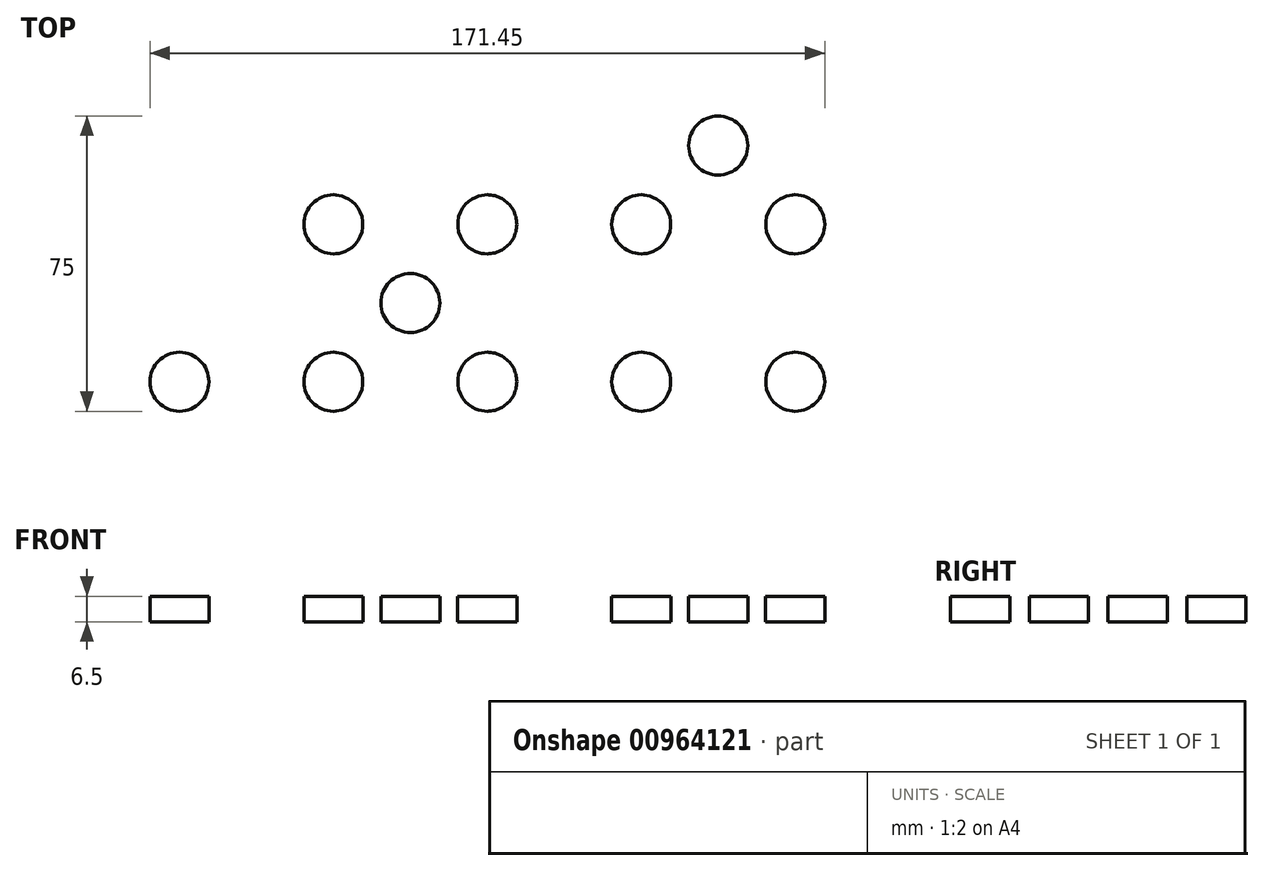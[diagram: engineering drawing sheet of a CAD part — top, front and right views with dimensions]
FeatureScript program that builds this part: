
annotation { "Feature Type Name" : "Feature", "Feature Type Description" : "" }
export const myFeature = defineFeature(function(context is Context, id is Id, definition is map)
    precondition{}
    {
        {
            var Q0;
            Q0=qCreatedBy(makeId("Top.planeOp"),FACE);
            var sketch = newSketch(context, id + "F0", { "sketchPlane" : qUnion([Q0])});
            skLineSegment(sketch, "E0.bottom", {"start": v(-100, 55) * mm, "end": v(100, 55) * mm});
            skLineSegment(sketch, "E0.top", {"start": v(-100, -55) * mm, "end": v(100, -55) * mm});
            skLineSegment(sketch, "E0.left", {"start": v(-100, 55) * mm, "end": v(-100, -55) * mm});
            skLineSegment(sketch, "E0.right", {"start": v(100, 55) * mm, "end": v(100, -55) * mm});
            skPoint(sketch, "E0.middle", {"position": v(0, 0) * mm});
            skSolve(sketch);
        }
        {
            var Q0;
            Q0=makeQuery(id+"F0.imprint","IMPRINT",FACE,{"disambiguationData":[TD([[makeQuery(id+"F0.imprint","IMPRINT",EDGE,{"derivedFrom":sQuery(id+"F0.wireOp",EDGE,"E0.bottom")}),-1.0]])]});
            extrude(context, id + "F1", {"entities" : qUnion([Q0]), "depth" : 6.5 * mm, "offsetDistance" : 25 * mm});
        }
        {
            var Q0;
            Q0=makeQuery(id+"F1.opExtrude","SWEPT_FACE",FACE,{"disambiguationData":[OSD([sQuery(id+"F0.wireOp",EDGE,"E0.left")])]});
            var sketch = newSketch(context, id + "F2", { "sketchPlane" : qUnion([Q0])});
            skLineSegment(sketch, "E1", {"start": v(-55, 3.25) * mm, "end": v(-35, 3.25) * mm});
            skLineSegment(sketch, "E2", {"start": v(-35, 3.25) * mm, "end": v(0, 3.25) * mm});
            skLineSegment(sketch, "E3", {"start": v(0, 3.25) * mm, "end": v(35, 3.25) * mm});
            skLineSegment(sketch, "E4", {"start": v(35, 3.25) * mm, "end": v(55, 3.25) * mm});
            skLineSegment(sketch, "E5.bottom", {"start": v(-39.75, 6.5) * mm, "end": v(-30.25, 6.5) * mm});
            skLineSegment(sketch, "E5.top", {"start": v(-39.75, 0) * mm, "end": v(-30.25, 0) * mm});
            skLineSegment(sketch, "E5.left", {"start": v(-39.75, 6.5) * mm, "end": v(-39.75, 0) * mm});
            skLineSegment(sketch, "E5.right", {"start": v(-30.25, 6.5) * mm, "end": v(-30.25, 0) * mm});
            skPoint(sketch, "E5.middle", {"position": v(-35, 3.25) * mm});
            skLineSegment(sketch, "E6.bottom", {"start": v(-4.75, 6.5) * mm, "end": v(4.75, 6.5) * mm});
            skLineSegment(sketch, "E6.top", {"start": v(-4.75, 0) * mm, "end": v(4.75, 0) * mm});
            skLineSegment(sketch, "E6.left", {"start": v(-4.75, 6.5) * mm, "end": v(-4.75, 0) * mm});
            skLineSegment(sketch, "E6.right", {"start": v(4.75, 6.5) * mm, "end": v(4.75, 0) * mm});
            skPoint(sketch, "E6.middle", {"position": v(0, 3.25) * mm});
            skLineSegment(sketch, "E7.bottom", {"start": v(39.75, 6.5) * mm, "end": v(30.25, 6.5) * mm});
            skLineSegment(sketch, "E7.top", {"start": v(39.75, 0) * mm, "end": v(30.25, 0) * mm});
            skLineSegment(sketch, "E7.left", {"start": v(39.75, 6.5) * mm, "end": v(39.75, 0) * mm});
            skLineSegment(sketch, "E7.right", {"start": v(30.25, 6.5) * mm, "end": v(30.25, 0) * mm});
            skPoint(sketch, "E7.middle", {"position": v(35, 3.25) * mm});
            skSolve(sketch);
        }
        {
            var Q0;
            {var subQ0=sQuery(id+"F2.wireOp",EDGE,"E5.bottom");Q0=makeQuery(id+"F2.imprint","IMPRINT",FACE,{"disambiguationData":[TD([[makeQuery(id+"F2.imprint","IMPRINT",EDGE,{"derivedFrom":subQ0}),-1.0]])]});}
            var Q1;
            {var subQ1=sQuery(id+"F2.wireOp",EDGE,"E5.top");Q1=makeQuery(id+"F2.imprint","IMPRINT",FACE,{"disambiguationData":[TD([[makeQuery(id+"F2.imprint","IMPRINT",EDGE,{"derivedFrom":subQ1}),1.0]])]});}
            var Q2;
            {var subQ1=sQuery(id+"F2.wireOp",EDGE,"E6.bottom");Q2=makeQuery(id+"F2.imprint","IMPRINT",FACE,{"disambiguationData":[TD([[makeQuery(id+"F2.imprint","IMPRINT",EDGE,{"derivedFrom":subQ1}),-1.0]])]});}
            var Q3;
            {var subQ0=sQuery(id+"F2.wireOp",EDGE,"E6.top");Q3=makeQuery(id+"F2.imprint","IMPRINT",FACE,{"disambiguationData":[TD([[makeQuery(id+"F2.imprint","IMPRINT",EDGE,{"derivedFrom":subQ0}),1.0]])]});}
            var Q4;
            {var subQ1=sQuery(id+"F2.wireOp",EDGE,"E7.bottom");Q4=makeQuery(id+"F2.imprint","IMPRINT",FACE,{"disambiguationData":[TD([[makeQuery(id+"F2.imprint","IMPRINT",EDGE,{"derivedFrom":subQ1}),-1.0]])]});}
            var Q5;
            {var subQ1=sQuery(id+"F2.wireOp",EDGE,"E7.top");Q5=makeQuery(id+"F2.imprint","IMPRINT",FACE,{"disambiguationData":[TD([[makeQuery(id+"F2.imprint","IMPRINT",EDGE,{"derivedFrom":subQ1}),1.0]])]});}
            extrude(context, id + "F3", {"entities" : qUnion([Q0, Q1, Q2, Q3, Q4, Q5]), "operationType" : NewBodyOperationType.ADD, "depth" : 6 * mm, "offsetDistance" : 25 * mm});
        }
        {
            var Q0;
            Q0=makeQuery(id+"F1.opExtrude","SWEPT_FACE",FACE,{"disambiguationData":[OSD([sQuery(id+"F0.wireOp",EDGE,"E0.right")])]});
            var sketch = newSketch(context, id + "F4", { "sketchPlane" : qUnion([Q0])});
            skLineSegment(sketch, "E8", {"start": v(-55, 3.25) * mm, "end": v(-35, 3.25) * mm});
            skLineSegment(sketch, "E9", {"start": v(-35, 3.25) * mm, "end": v(0, 3.25) * mm});
            skLineSegment(sketch, "E10", {"start": v(0, 3.25) * mm, "end": v(35, 3.25) * mm});
            skLineSegment(sketch, "E11.bottom", {"start": v(-39.75, 6.5) * mm, "end": v(-30.25, 6.5) * mm});
            skLineSegment(sketch, "E11.top", {"start": v(-39.75, 0) * mm, "end": v(-30.25, 0) * mm});
            skLineSegment(sketch, "E11.left", {"start": v(-39.75, 6.5) * mm, "end": v(-39.75, 0) * mm});
            skLineSegment(sketch, "E11.right", {"start": v(-30.25, 6.5) * mm, "end": v(-30.25, 0) * mm});
            skPoint(sketch, "E11.middle", {"position": v(-35, 3.25) * mm});
            skLineSegment(sketch, "E12.bottom", {"start": v(-4.75, 6.5) * mm, "end": v(4.75, 6.5) * mm});
            skLineSegment(sketch, "E12.top", {"start": v(-4.75, 0) * mm, "end": v(4.75, 0) * mm});
            skLineSegment(sketch, "E12.left", {"start": v(-4.75, 6.5) * mm, "end": v(-4.75, 0) * mm});
            skLineSegment(sketch, "E12.right", {"start": v(4.75, 6.5) * mm, "end": v(4.75, 0) * mm});
            skPoint(sketch, "E12.middle", {"position": v(0, 3.25) * mm});
            skLineSegment(sketch, "E13.bottom", {"start": v(39.75, 6.5) * mm, "end": v(30.25, 6.5) * mm});
            skLineSegment(sketch, "E13.top", {"start": v(39.75, 0) * mm, "end": v(30.25, 0) * mm});
            skLineSegment(sketch, "E13.left", {"start": v(39.75, 6.5) * mm, "end": v(39.75, 0) * mm});
            skLineSegment(sketch, "E13.right", {"start": v(30.25, 6.5) * mm, "end": v(30.25, 0) * mm});
            skPoint(sketch, "E13.middle", {"position": v(35, 3.25) * mm});
            skSolve(sketch);
        }
        {
            var Q0;
            {var subQ1=sQuery(id+"F4.wireOp",EDGE,"E11.bottom");Q0=makeQuery(id+"F4.imprint","IMPRINT",FACE,{"disambiguationData":[TD([[makeQuery(id+"F4.imprint","IMPRINT",EDGE,{"derivedFrom":subQ1}),1.0]])]});}
            var Q1;
            {var subQ1=sQuery(id+"F4.wireOp",EDGE,"E11.top");Q1=makeQuery(id+"F4.imprint","IMPRINT",FACE,{"disambiguationData":[TD([[makeQuery(id+"F4.imprint","IMPRINT",EDGE,{"derivedFrom":subQ1}),-1.0]])]});}
            var Q2;
            {var subQ0=sQuery(id+"F4.wireOp",EDGE,"E12.bottom");Q2=makeQuery(id+"F4.imprint","IMPRINT",FACE,{"disambiguationData":[TD([[makeQuery(id+"F4.imprint","IMPRINT",EDGE,{"derivedFrom":subQ0}),1.0]])]});}
            var Q3;
            {var subQ1=sQuery(id+"F4.wireOp",EDGE,"E12.top");Q3=makeQuery(id+"F4.imprint","IMPRINT",FACE,{"disambiguationData":[TD([[makeQuery(id+"F4.imprint","IMPRINT",EDGE,{"derivedFrom":subQ1}),-1.0]])]});}
            var Q4;
            {var subQ1=sQuery(id+"F4.wireOp",EDGE,"E13.bottom");Q4=makeQuery(id+"F4.imprint","IMPRINT",FACE,{"disambiguationData":[TD([[makeQuery(id+"F4.imprint","IMPRINT",EDGE,{"derivedFrom":subQ1}),1.0]])]});}
            extrude(context, id + "F5", {"entities" : qUnion([Q0, Q1, Q2, Q3, Q4]), "operationType" : NewBodyOperationType.ADD, "depth" : 6 * mm, "offsetDistance" : 25 * mm});
        }
        {
            var Q0;
            Q0=makeQuery(id+"F5.boolean.opBoolean","MERGE",FACE,{"derivedFrom":[makeQuery(id+"F3.boolean.opBoolean","MERGE",FACE,{"derivedFrom":[makeQuery(id+"F1.opExtrude","CAP_FACE",FACE,{"disambiguationData":[OSD([sQuery(id+"F0.wireOp",EDGE,"E0.bottom"),sQuery(id+"F0.wireOp",EDGE,"E0.top"),sQuery(id+"F0.wireOp",EDGE,"E0.left"),sQuery(id+"F0.wireOp",EDGE,"E0.right")])],"isStart":false}),makeQuery(id+"F3.opExtrude","SWEPT_FACE",FACE,{"disambiguationData":[OSD([sQuery(id+"F2.wireOp",EDGE,"E5.bottom")])]}),makeQuery(id+"F3.opExtrude","SWEPT_FACE",FACE,{"disambiguationData":[OSD([sQuery(id+"F2.wireOp",EDGE,"E6.bottom")])]}),makeQuery(id+"F3.opExtrude","SWEPT_FACE",FACE,{"disambiguationData":[OSD([sQuery(id+"F2.wireOp",EDGE,"E7.bottom")])]})]}),makeQuery(id+"F5.opExtrude","SWEPT_FACE",FACE,{"disambiguationData":[OSD([sQuery(id+"F4.wireOp",EDGE,"E11.bottom")])]}),makeQuery(id+"F5.opExtrude","SWEPT_FACE",FACE,{"disambiguationData":[OSD([sQuery(id+"F4.wireOp",EDGE,"E12.bottom")])]}),makeQuery(id+"F5.opExtrude","SWEPT_FACE",FACE,{"disambiguationData":[OSD([sQuery(id+"F4.wireOp",EDGE,"E13.bottom")])]})]});
            var sketch = newSketch(context, id + "F6", { "sketchPlane" : qUnion([Q0])});
            skLineSegment(sketch, "E14", {"start": v(-88, 55) * mm, "end": v(-88, 40) * mm});
            skLineSegment(sketch, "E15", {"start": v(-88, 40) * mm, "end": v(-88, 20) * mm});
            skLineSegment(sketch, "E16", {"start": v(-88, 20) * mm, "end": v(-88, 0) * mm});
            skLineSegment(sketch, "E17", {"start": v(-88, 0) * mm, "end": v(-88, -20) * mm});
            skLineSegment(sketch, "E18", {"start": v(-88, -20) * mm, "end": v(-88, -40) * mm});
            skCircle(sketch, "E19", {"center": v(-88, 40) * mm, "radius": 7.5 * mm});
            skCircle(sketch, "E20", {"center": v(-88, 20) * mm, "radius": 7.5 * mm});
            skCircle(sketch, "E21", {"center": v(-88, 0) * mm, "radius": 7.5 * mm});
            skCircle(sketch, "E22", {"center": v(-88, -20) * mm, "radius": 7.5 * mm});
            skCircle(sketch, "E23", {"center": v(-88, -40) * mm, "radius": 7.5 * mm});
            skLineSegment(sketch, "E24", {"start": v(-68.44, 55) * mm, "end": v(-68.44, -55) * mm});
            skLineSegment(sketch, "E25", {"start": v(-48.89, 55) * mm, "end": v(-48.89, -55) * mm});
            skLineSegment(sketch, "E26", {"start": v(-29.33, 55) * mm, "end": v(-29.33, -55) * mm});
            skLineSegment(sketch, "E27", {"start": v(-9.78, -55) * mm, "end": v(-9.78, 55) * mm});
            skLineSegment(sketch, "E28", {"start": v(9.78, 55) * mm, "end": v(9.78, -55) * mm});
            skLineSegment(sketch, "E29", {"start": v(29.33, -55) * mm, "end": v(29.33, 55) * mm});
            skLineSegment(sketch, "E30", {"start": v(68.44, 55) * mm, "end": v(68.44, -55) * mm});
            skLineSegment(sketch, "E31", {"start": v(48.89, 55) * mm, "end": v(48.89, -55) * mm});
            skLineSegment(sketch, "E32", {"start": v(88, 55) * mm, "end": v(88, -55) * mm});
            skCircle(sketch, "E33", {"center": v(-68.44, 40) * mm, "radius": 7.99 * mm});
            skCircle(sketch, "E34", {"center": v(-68.44, 20) * mm, "radius": 7.5 * mm});
            skCircle(sketch, "E35", {"center": v(-68.44, 0) * mm, "radius": 7.5 * mm});
            skCircle(sketch, "E36", {"center": v(-68.44, -20) * mm, "radius": 7.5 * mm});
            skCircle(sketch, "E37", {"center": v(-68.44, -40) * mm, "radius": 7.5 * mm});
            skCircle(sketch, "E38.MirrorC", {"center": v(-48.89, 40) * mm, "radius": 7.5 * mm});
            skCircle(sketch, "E39.MirrorC", {"center": v(-48.89, 20) * mm, "radius": 7.5 * mm});
            skCircle(sketch, "E40.MirrorC", {"center": v(-48.89, 0) * mm, "radius": 7.5 * mm});
            skCircle(sketch, "E41.MirrorC", {"center": v(-48.89, -20) * mm, "radius": 7.5 * mm});
            skCircle(sketch, "E42.MirrorC", {"center": v(-48.89, -40) * mm, "radius": 7.5 * mm});
            skCircle(sketch, "E43.MirrorC", {"center": v(-29.33, 40) * mm, "radius": 7.99 * mm});
            skCircle(sketch, "E44.MirrorC", {"center": v(-29.33, 20) * mm, "radius": 7.5 * mm});
            skCircle(sketch, "E45.MirrorC", {"center": v(-29.33, 0) * mm, "radius": 7.5 * mm});
            skCircle(sketch, "E46.MirrorC", {"center": v(-29.33, -20) * mm, "radius": 7.5 * mm});
            skCircle(sketch, "E47.MirrorC", {"center": v(-29.33, -40) * mm, "radius": 7.5 * mm});
            skCircle(sketch, "E48.MirrorC", {"center": v(-9.78, 40) * mm, "radius": 7.5 * mm});
            skCircle(sketch, "E49.MirrorC", {"center": v(-9.78, 20) * mm, "radius": 7.5 * mm});
            skCircle(sketch, "E50.MirrorC", {"center": v(-9.78, 0) * mm, "radius": 7.5 * mm});
            skCircle(sketch, "E51.MirrorC", {"center": v(-9.78, -40) * mm, "radius": 7.5 * mm});
            skCircle(sketch, "E52.MirrorC", {"center": v(-9.78, -20) * mm, "radius": 7.5 * mm});
            skCircle(sketch, "E53.MirrorC", {"center": v(29.33, 40) * mm, "radius": 7.5 * mm});
            skCircle(sketch, "E54.MirrorC", {"center": v(29.33, 20) * mm, "radius": 7.5 * mm});
            skCircle(sketch, "E55.MirrorC", {"center": v(29.33, 0) * mm, "radius": 7.5 * mm});
            skCircle(sketch, "E56.MirrorC", {"center": v(29.33, -20) * mm, "radius": 7.5 * mm});
            skCircle(sketch, "E57.MirrorC", {"center": v(29.33, -40) * mm, "radius": 7.5 * mm});
            skCircle(sketch, "E58.MirrorC", {"center": v(9.78, 20) * mm, "radius": 7.5 * mm});
            skCircle(sketch, "E59.MirrorC", {"center": v(9.78, 0) * mm, "radius": 7.5 * mm});
            skCircle(sketch, "E60.MirrorC", {"center": v(9.78, 40) * mm, "radius": 7.99 * mm});
            skCircle(sketch, "E61.MirrorC", {"center": v(9.78, -20) * mm, "radius": 7.5 * mm});
            skCircle(sketch, "E62.MirrorC", {"center": v(9.78, -40) * mm, "radius": 7.5 * mm});
            skCircle(sketch, "E63.MirrorC", {"center": v(48.89, 40) * mm, "radius": 7.99 * mm});
            skCircle(sketch, "E64.MirrorC", {"center": v(48.89, 20) * mm, "radius": 7.5 * mm});
            skCircle(sketch, "E65.MirrorC", {"center": v(48.89, 0) * mm, "radius": 7.5 * mm});
            skCircle(sketch, "E66.MirrorC", {"center": v(48.89, -20) * mm, "radius": 7.5 * mm});
            skCircle(sketch, "E67.MirrorC", {"center": v(48.89, -40) * mm, "radius": 7.5 * mm});
            skCircle(sketch, "E68.MirrorC", {"center": v(68.44, 40) * mm, "radius": 7.5 * mm});
            skCircle(sketch, "E69.MirrorC", {"center": v(68.44, 20) * mm, "radius": 7.5 * mm});
            skCircle(sketch, "E70.MirrorC", {"center": v(68.44, 0) * mm, "radius": 7.5 * mm});
            skCircle(sketch, "E71.MirrorC", {"center": v(68.44, -20) * mm, "radius": 7.5 * mm});
            skCircle(sketch, "E72.MirrorC", {"center": v(68.44, -40) * mm, "radius": 7.5 * mm});
            skCircle(sketch, "E73.MirrorC", {"center": v(88, 40) * mm, "radius": 7.99 * mm});
            skCircle(sketch, "E74.MirrorC", {"center": v(88, 20) * mm, "radius": 7.5 * mm});
            skCircle(sketch, "E75.MirrorC", {"center": v(88, 0) * mm, "radius": 7.5 * mm});
            skCircle(sketch, "E76.MirrorC", {"center": v(88, -20) * mm, "radius": 7.5 * mm});
            skCircle(sketch, "E77.MirrorC", {"center": v(88, -40) * mm, "radius": 7.5 * mm});
            skSolve(sketch);
        }
        {
            var Q0;
            {var subQ0=sQuery(id+"F6.wireOp",EDGE,"E15");var subQ1=sQuery(id+"F6.wireOp",EDGE,"E14");var subQ2=makeQuery(id+"F6.imprint","INTERSECT",VERTEX,{"derivedFrom":[subQ1,subQ0]});Q0=makeQuery(id+"F6.imprint","IMPRINT",FACE,{"disambiguationData":[TD([[makeQuery(id+"F6.imprint","IMPRINT",EDGE,{"disambiguationData":[TD([[subQ2,1.0]])],"derivedFrom":subQ1}),-1.0]])]});}
            var Q1;
            {var subQ0=sQuery(id+"F6.wireOp",EDGE,"E15");var subQ1=sQuery(id+"F6.wireOp",EDGE,"E14");var subQ2=makeQuery(id+"F6.imprint","INTERSECT",VERTEX,{"derivedFrom":[subQ1,subQ0]});Q1=makeQuery(id+"F6.imprint","IMPRINT",FACE,{"disambiguationData":[TD([[makeQuery(id+"F6.imprint","IMPRINT",EDGE,{"disambiguationData":[TD([[subQ2,1.0]])],"derivedFrom":subQ1}),1.0]])]});}
            var Q2;
            {var subQ0=sQuery(id+"F6.wireOp",EDGE,"E33");var subQ1=sQuery(id+"F6.wireOp",EDGE,"E24");var subQ2=makeQuery(id+"F6.imprint","INTERSECT",VERTEX,{"disambiguationData":[OD(0.0)],"derivedFrom":[subQ1,subQ0]});Q2=makeQuery(id+"F6.imprint","IMPRINT",FACE,{"disambiguationData":[TD([[makeQuery(id+"F6.imprint","IMPRINT",EDGE,{"disambiguationData":[TD([[subQ2,-1.0]])],"derivedFrom":subQ1}),-1.0]])]});}
            var Q3;
            {var subQ0=sQuery(id+"F6.wireOp",EDGE,"E33");var subQ1=sQuery(id+"F6.wireOp",EDGE,"E24");var subQ2=makeQuery(id+"F6.imprint","INTERSECT",VERTEX,{"disambiguationData":[OD(0.0)],"derivedFrom":[subQ1,subQ0]});Q3=makeQuery(id+"F6.imprint","IMPRINT",FACE,{"disambiguationData":[TD([[makeQuery(id+"F6.imprint","IMPRINT",EDGE,{"disambiguationData":[TD([[subQ2,-1.0]])],"derivedFrom":subQ1}),1.0]])]});}
            var Q4;
            {var subQ0=sQuery(id+"F6.wireOp",EDGE,"E38.MirrorC");var subQ1=sQuery(id+"F6.wireOp",EDGE,"E25");var subQ2=makeQuery(id+"F6.imprint","INTERSECT",VERTEX,{"disambiguationData":[OD(0.0)],"derivedFrom":[subQ1,subQ0]});Q4=makeQuery(id+"F6.imprint","IMPRINT",FACE,{"disambiguationData":[TD([[makeQuery(id+"F6.imprint","IMPRINT",EDGE,{"disambiguationData":[TD([[subQ2,-1.0]])],"derivedFrom":subQ1}),-1.0]])]});}
            var Q5;
            {var subQ0=sQuery(id+"F6.wireOp",EDGE,"E38.MirrorC");var subQ1=sQuery(id+"F6.wireOp",EDGE,"E25");var subQ2=makeQuery(id+"F6.imprint","INTERSECT",VERTEX,{"disambiguationData":[OD(0.0)],"derivedFrom":[subQ1,subQ0]});Q5=makeQuery(id+"F6.imprint","IMPRINT",FACE,{"disambiguationData":[TD([[makeQuery(id+"F6.imprint","IMPRINT",EDGE,{"disambiguationData":[TD([[subQ2,-1.0]])],"derivedFrom":subQ1}),1.0]])]});}
            var Q6;
            {var subQ0=sQuery(id+"F6.wireOp",EDGE,"E43.MirrorC");var subQ1=sQuery(id+"F6.wireOp",EDGE,"E26");var subQ2=makeQuery(id+"F6.imprint","INTERSECT",VERTEX,{"disambiguationData":[OD(0.0)],"derivedFrom":[subQ1,subQ0]});Q6=makeQuery(id+"F6.imprint","IMPRINT",FACE,{"disambiguationData":[TD([[makeQuery(id+"F6.imprint","IMPRINT",EDGE,{"disambiguationData":[TD([[subQ2,-1.0]])],"derivedFrom":subQ1}),-1.0]])]});}
            var Q7;
            {var subQ0=sQuery(id+"F6.wireOp",EDGE,"E43.MirrorC");var subQ1=sQuery(id+"F6.wireOp",EDGE,"E26");var subQ2=makeQuery(id+"F6.imprint","INTERSECT",VERTEX,{"disambiguationData":[OD(0.0)],"derivedFrom":[subQ1,subQ0]});Q7=makeQuery(id+"F6.imprint","IMPRINT",FACE,{"disambiguationData":[TD([[makeQuery(id+"F6.imprint","IMPRINT",EDGE,{"disambiguationData":[TD([[subQ2,-1.0]])],"derivedFrom":subQ1}),1.0]])]});}
            var Q8;
            {var subQ0=sQuery(id+"F6.wireOp",EDGE,"E48.MirrorC");var subQ1=sQuery(id+"F6.wireOp",EDGE,"E27");var subQ2=makeQuery(id+"F6.imprint","INTERSECT",VERTEX,{"disambiguationData":[OD(0.0)],"derivedFrom":[subQ1,subQ0]});Q8=makeQuery(id+"F6.imprint","IMPRINT",FACE,{"disambiguationData":[TD([[makeQuery(id+"F6.imprint","IMPRINT",EDGE,{"disambiguationData":[TD([[subQ2,-1.0]])],"derivedFrom":subQ1}),1.0]])]});}
            var Q9;
            {var subQ0=sQuery(id+"F6.wireOp",EDGE,"E48.MirrorC");var subQ1=sQuery(id+"F6.wireOp",EDGE,"E27");var subQ2=makeQuery(id+"F6.imprint","INTERSECT",VERTEX,{"disambiguationData":[OD(0.0)],"derivedFrom":[subQ1,subQ0]});Q9=makeQuery(id+"F6.imprint","IMPRINT",FACE,{"disambiguationData":[TD([[makeQuery(id+"F6.imprint","IMPRINT",EDGE,{"disambiguationData":[TD([[subQ2,-1.0]])],"derivedFrom":subQ1}),-1.0]])]});}
            var Q10;
            {var subQ0=sQuery(id+"F6.wireOp",EDGE,"E60.MirrorC");var subQ1=sQuery(id+"F6.wireOp",EDGE,"E28");var subQ2=makeQuery(id+"F6.imprint","INTERSECT",VERTEX,{"disambiguationData":[OD(0.0)],"derivedFrom":[subQ1,subQ0]});Q10=makeQuery(id+"F6.imprint","IMPRINT",FACE,{"disambiguationData":[TD([[makeQuery(id+"F6.imprint","IMPRINT",EDGE,{"disambiguationData":[TD([[subQ2,-1.0]])],"derivedFrom":subQ1}),-1.0]])]});}
            var Q11;
            {var subQ0=sQuery(id+"F6.wireOp",EDGE,"E60.MirrorC");var subQ1=sQuery(id+"F6.wireOp",EDGE,"E28");var subQ2=makeQuery(id+"F6.imprint","INTERSECT",VERTEX,{"disambiguationData":[OD(0.0)],"derivedFrom":[subQ1,subQ0]});Q11=makeQuery(id+"F6.imprint","IMPRINT",FACE,{"disambiguationData":[TD([[makeQuery(id+"F6.imprint","IMPRINT",EDGE,{"disambiguationData":[TD([[subQ2,-1.0]])],"derivedFrom":subQ1}),1.0]])]});}
            var Q12;
            {var subQ0=sQuery(id+"F6.wireOp",EDGE,"E53.MirrorC");var subQ1=sQuery(id+"F6.wireOp",EDGE,"E29");var subQ2=makeQuery(id+"F6.imprint","INTERSECT",VERTEX,{"disambiguationData":[OD(0.0)],"derivedFrom":[subQ1,subQ0]});Q12=makeQuery(id+"F6.imprint","IMPRINT",FACE,{"disambiguationData":[TD([[makeQuery(id+"F6.imprint","IMPRINT",EDGE,{"disambiguationData":[TD([[subQ2,-1.0]])],"derivedFrom":subQ1}),1.0]])]});}
            var Q13;
            {var subQ0=sQuery(id+"F6.wireOp",EDGE,"E53.MirrorC");var subQ1=sQuery(id+"F6.wireOp",EDGE,"E29");var subQ2=makeQuery(id+"F6.imprint","INTERSECT",VERTEX,{"disambiguationData":[OD(0.0)],"derivedFrom":[subQ1,subQ0]});Q13=makeQuery(id+"F6.imprint","IMPRINT",FACE,{"disambiguationData":[TD([[makeQuery(id+"F6.imprint","IMPRINT",EDGE,{"disambiguationData":[TD([[subQ2,-1.0]])],"derivedFrom":subQ1}),-1.0]])]});}
            var Q14;
            {var subQ0=sQuery(id+"F6.wireOp",EDGE,"E63.MirrorC");var subQ1=sQuery(id+"F6.wireOp",EDGE,"E31");var subQ2=makeQuery(id+"F6.imprint","INTERSECT",VERTEX,{"disambiguationData":[OD(0.0)],"derivedFrom":[subQ1,subQ0]});Q14=makeQuery(id+"F6.imprint","IMPRINT",FACE,{"disambiguationData":[TD([[makeQuery(id+"F6.imprint","IMPRINT",EDGE,{"disambiguationData":[TD([[subQ2,-1.0]])],"derivedFrom":subQ1}),-1.0]])]});}
            var Q15;
            {var subQ0=sQuery(id+"F6.wireOp",EDGE,"E63.MirrorC");var subQ1=sQuery(id+"F6.wireOp",EDGE,"E31");var subQ2=makeQuery(id+"F6.imprint","INTERSECT",VERTEX,{"disambiguationData":[OD(0.0)],"derivedFrom":[subQ1,subQ0]});Q15=makeQuery(id+"F6.imprint","IMPRINT",FACE,{"disambiguationData":[TD([[makeQuery(id+"F6.imprint","IMPRINT",EDGE,{"disambiguationData":[TD([[subQ2,-1.0]])],"derivedFrom":subQ1}),1.0]])]});}
            var Q16;
            {var subQ0=sQuery(id+"F6.wireOp",EDGE,"E68.MirrorC");var subQ1=sQuery(id+"F6.wireOp",EDGE,"E30");var subQ2=makeQuery(id+"F6.imprint","INTERSECT",VERTEX,{"disambiguationData":[OD(0.0)],"derivedFrom":[subQ1,subQ0]});Q16=makeQuery(id+"F6.imprint","IMPRINT",FACE,{"disambiguationData":[TD([[makeQuery(id+"F6.imprint","IMPRINT",EDGE,{"disambiguationData":[TD([[subQ2,-1.0]])],"derivedFrom":subQ1}),-1.0]])]});}
            var Q17;
            {var subQ0=sQuery(id+"F6.wireOp",EDGE,"E68.MirrorC");var subQ1=sQuery(id+"F6.wireOp",EDGE,"E30");var subQ2=makeQuery(id+"F6.imprint","INTERSECT",VERTEX,{"disambiguationData":[OD(0.0)],"derivedFrom":[subQ1,subQ0]});Q17=makeQuery(id+"F6.imprint","IMPRINT",FACE,{"disambiguationData":[TD([[makeQuery(id+"F6.imprint","IMPRINT",EDGE,{"disambiguationData":[TD([[subQ2,-1.0]])],"derivedFrom":subQ1}),1.0]])]});}
            var Q18;
            {var subQ0=sQuery(id+"F6.wireOp",EDGE,"E73.MirrorC");var subQ1=sQuery(id+"F6.wireOp",EDGE,"E32");var subQ2=makeQuery(id+"F6.imprint","INTERSECT",VERTEX,{"disambiguationData":[OD(0.0)],"derivedFrom":[subQ1,subQ0]});Q18=makeQuery(id+"F6.imprint","IMPRINT",FACE,{"disambiguationData":[TD([[makeQuery(id+"F6.imprint","IMPRINT",EDGE,{"disambiguationData":[TD([[subQ2,-1.0]])],"derivedFrom":subQ1}),-1.0]])]});}
            var Q19;
            {var subQ0=sQuery(id+"F6.wireOp",EDGE,"E73.MirrorC");var subQ1=sQuery(id+"F6.wireOp",EDGE,"E32");var subQ2=makeQuery(id+"F6.imprint","INTERSECT",VERTEX,{"disambiguationData":[OD(0.0)],"derivedFrom":[subQ1,subQ0]});Q19=makeQuery(id+"F6.imprint","IMPRINT",FACE,{"disambiguationData":[TD([[makeQuery(id+"F6.imprint","IMPRINT",EDGE,{"disambiguationData":[TD([[subQ2,-1.0]])],"derivedFrom":subQ1}),1.0]])]});}
            var Q20;
            {var subQ0=sQuery(id+"F6.wireOp",EDGE,"E74.MirrorC");var subQ1=sQuery(id+"F6.wireOp",EDGE,"E32");var subQ2=makeQuery(id+"F6.imprint","INTERSECT",VERTEX,{"disambiguationData":[OD(0.0)],"derivedFrom":[subQ1,subQ0]});Q20=makeQuery(id+"F6.imprint","IMPRINT",FACE,{"disambiguationData":[TD([[makeQuery(id+"F6.imprint","IMPRINT",EDGE,{"disambiguationData":[TD([[subQ2,-1.0]])],"derivedFrom":subQ1}),1.0]])]});}
            var Q21;
            {var subQ0=sQuery(id+"F6.wireOp",EDGE,"E74.MirrorC");var subQ1=sQuery(id+"F6.wireOp",EDGE,"E32");var subQ2=makeQuery(id+"F6.imprint","INTERSECT",VERTEX,{"disambiguationData":[OD(0.0)],"derivedFrom":[subQ1,subQ0]});Q21=makeQuery(id+"F6.imprint","IMPRINT",FACE,{"disambiguationData":[TD([[makeQuery(id+"F6.imprint","IMPRINT",EDGE,{"disambiguationData":[TD([[subQ2,-1.0]])],"derivedFrom":subQ1}),-1.0]])]});}
            var Q22;
            {var subQ0=sQuery(id+"F6.wireOp",EDGE,"E69.MirrorC");var subQ1=sQuery(id+"F6.wireOp",EDGE,"E30");var subQ2=makeQuery(id+"F6.imprint","INTERSECT",VERTEX,{"disambiguationData":[OD(0.0)],"derivedFrom":[subQ1,subQ0]});Q22=makeQuery(id+"F6.imprint","IMPRINT",FACE,{"disambiguationData":[TD([[makeQuery(id+"F6.imprint","IMPRINT",EDGE,{"disambiguationData":[TD([[subQ2,-1.0]])],"derivedFrom":subQ1}),1.0]])]});}
            var Q23;
            {var subQ0=sQuery(id+"F6.wireOp",EDGE,"E69.MirrorC");var subQ1=sQuery(id+"F6.wireOp",EDGE,"E30");var subQ2=makeQuery(id+"F6.imprint","INTERSECT",VERTEX,{"disambiguationData":[OD(0.0)],"derivedFrom":[subQ1,subQ0]});Q23=makeQuery(id+"F6.imprint","IMPRINT",FACE,{"disambiguationData":[TD([[makeQuery(id+"F6.imprint","IMPRINT",EDGE,{"disambiguationData":[TD([[subQ2,-1.0]])],"derivedFrom":subQ1}),-1.0]])]});}
            var Q24;
            {var subQ0=sQuery(id+"F6.wireOp",EDGE,"E64.MirrorC");var subQ1=sQuery(id+"F6.wireOp",EDGE,"E31");var subQ2=makeQuery(id+"F6.imprint","INTERSECT",VERTEX,{"disambiguationData":[OD(0.0)],"derivedFrom":[subQ1,subQ0]});Q24=makeQuery(id+"F6.imprint","IMPRINT",FACE,{"disambiguationData":[TD([[makeQuery(id+"F6.imprint","IMPRINT",EDGE,{"disambiguationData":[TD([[subQ2,-1.0]])],"derivedFrom":subQ1}),1.0]])]});}
            var Q25;
            {var subQ0=sQuery(id+"F6.wireOp",EDGE,"E64.MirrorC");var subQ1=sQuery(id+"F6.wireOp",EDGE,"E31");var subQ2=makeQuery(id+"F6.imprint","INTERSECT",VERTEX,{"disambiguationData":[OD(0.0)],"derivedFrom":[subQ1,subQ0]});Q25=makeQuery(id+"F6.imprint","IMPRINT",FACE,{"disambiguationData":[TD([[makeQuery(id+"F6.imprint","IMPRINT",EDGE,{"disambiguationData":[TD([[subQ2,-1.0]])],"derivedFrom":subQ1}),-1.0]])]});}
            var Q26;
            {var subQ0=sQuery(id+"F6.wireOp",EDGE,"E54.MirrorC");var subQ1=sQuery(id+"F6.wireOp",EDGE,"E29");var subQ2=makeQuery(id+"F6.imprint","INTERSECT",VERTEX,{"disambiguationData":[OD(0.0)],"derivedFrom":[subQ1,subQ0]});Q26=makeQuery(id+"F6.imprint","IMPRINT",FACE,{"disambiguationData":[TD([[makeQuery(id+"F6.imprint","IMPRINT",EDGE,{"disambiguationData":[TD([[subQ2,-1.0]])],"derivedFrom":subQ1}),-1.0]])]});}
            var Q27;
            {var subQ0=sQuery(id+"F6.wireOp",EDGE,"E54.MirrorC");var subQ1=sQuery(id+"F6.wireOp",EDGE,"E29");var subQ2=makeQuery(id+"F6.imprint","INTERSECT",VERTEX,{"disambiguationData":[OD(0.0)],"derivedFrom":[subQ1,subQ0]});Q27=makeQuery(id+"F6.imprint","IMPRINT",FACE,{"disambiguationData":[TD([[makeQuery(id+"F6.imprint","IMPRINT",EDGE,{"disambiguationData":[TD([[subQ2,-1.0]])],"derivedFrom":subQ1}),1.0]])]});}
            var Q28;
            {var subQ0=sQuery(id+"F6.wireOp",EDGE,"E58.MirrorC");var subQ1=sQuery(id+"F6.wireOp",EDGE,"E28");var subQ2=makeQuery(id+"F6.imprint","INTERSECT",VERTEX,{"disambiguationData":[OD(0.0)],"derivedFrom":[subQ1,subQ0]});Q28=makeQuery(id+"F6.imprint","IMPRINT",FACE,{"disambiguationData":[TD([[makeQuery(id+"F6.imprint","IMPRINT",EDGE,{"disambiguationData":[TD([[subQ2,-1.0]])],"derivedFrom":subQ1}),1.0]])]});}
            var Q29;
            {var subQ0=sQuery(id+"F6.wireOp",EDGE,"E58.MirrorC");var subQ1=sQuery(id+"F6.wireOp",EDGE,"E28");var subQ2=makeQuery(id+"F6.imprint","INTERSECT",VERTEX,{"disambiguationData":[OD(0.0)],"derivedFrom":[subQ1,subQ0]});Q29=makeQuery(id+"F6.imprint","IMPRINT",FACE,{"disambiguationData":[TD([[makeQuery(id+"F6.imprint","IMPRINT",EDGE,{"disambiguationData":[TD([[subQ2,-1.0]])],"derivedFrom":subQ1}),-1.0]])]});}
            var Q30;
            {var subQ0=sQuery(id+"F6.wireOp",EDGE,"E49.MirrorC");var subQ1=sQuery(id+"F6.wireOp",EDGE,"E27");var subQ2=makeQuery(id+"F6.imprint","INTERSECT",VERTEX,{"disambiguationData":[OD(0.0)],"derivedFrom":[subQ1,subQ0]});Q30=makeQuery(id+"F6.imprint","IMPRINT",FACE,{"disambiguationData":[TD([[makeQuery(id+"F6.imprint","IMPRINT",EDGE,{"disambiguationData":[TD([[subQ2,-1.0]])],"derivedFrom":subQ1}),-1.0]])]});}
            var Q31;
            {var subQ0=sQuery(id+"F6.wireOp",EDGE,"E49.MirrorC");var subQ1=sQuery(id+"F6.wireOp",EDGE,"E27");var subQ2=makeQuery(id+"F6.imprint","INTERSECT",VERTEX,{"disambiguationData":[OD(0.0)],"derivedFrom":[subQ1,subQ0]});Q31=makeQuery(id+"F6.imprint","IMPRINT",FACE,{"disambiguationData":[TD([[makeQuery(id+"F6.imprint","IMPRINT",EDGE,{"disambiguationData":[TD([[subQ2,-1.0]])],"derivedFrom":subQ1}),1.0]])]});}
            var Q32;
            {var subQ0=sQuery(id+"F6.wireOp",EDGE,"E44.MirrorC");var subQ1=sQuery(id+"F6.wireOp",EDGE,"E26");var subQ2=makeQuery(id+"F6.imprint","INTERSECT",VERTEX,{"disambiguationData":[OD(0.0)],"derivedFrom":[subQ1,subQ0]});Q32=makeQuery(id+"F6.imprint","IMPRINT",FACE,{"disambiguationData":[TD([[makeQuery(id+"F6.imprint","IMPRINT",EDGE,{"disambiguationData":[TD([[subQ2,-1.0]])],"derivedFrom":subQ1}),1.0]])]});}
            var Q33;
            {var subQ0=sQuery(id+"F6.wireOp",EDGE,"E44.MirrorC");var subQ1=sQuery(id+"F6.wireOp",EDGE,"E26");var subQ2=makeQuery(id+"F6.imprint","INTERSECT",VERTEX,{"disambiguationData":[OD(0.0)],"derivedFrom":[subQ1,subQ0]});Q33=makeQuery(id+"F6.imprint","IMPRINT",FACE,{"disambiguationData":[TD([[makeQuery(id+"F6.imprint","IMPRINT",EDGE,{"disambiguationData":[TD([[subQ2,-1.0]])],"derivedFrom":subQ1}),-1.0]])]});}
            var Q34;
            {var subQ0=sQuery(id+"F6.wireOp",EDGE,"E39.MirrorC");var subQ1=sQuery(id+"F6.wireOp",EDGE,"E25");var subQ2=makeQuery(id+"F6.imprint","INTERSECT",VERTEX,{"disambiguationData":[OD(0.0)],"derivedFrom":[subQ1,subQ0]});Q34=makeQuery(id+"F6.imprint","IMPRINT",FACE,{"disambiguationData":[TD([[makeQuery(id+"F6.imprint","IMPRINT",EDGE,{"disambiguationData":[TD([[subQ2,-1.0]])],"derivedFrom":subQ1}),1.0]])]});}
            var Q35;
            {var subQ0=sQuery(id+"F6.wireOp",EDGE,"E39.MirrorC");var subQ1=sQuery(id+"F6.wireOp",EDGE,"E25");var subQ2=makeQuery(id+"F6.imprint","INTERSECT",VERTEX,{"disambiguationData":[OD(0.0)],"derivedFrom":[subQ1,subQ0]});Q35=makeQuery(id+"F6.imprint","IMPRINT",FACE,{"disambiguationData":[TD([[makeQuery(id+"F6.imprint","IMPRINT",EDGE,{"disambiguationData":[TD([[subQ2,-1.0]])],"derivedFrom":subQ1}),-1.0]])]});}
            var Q36;
            {var subQ0=sQuery(id+"F6.wireOp",EDGE,"E34");var subQ1=sQuery(id+"F6.wireOp",EDGE,"E24");var subQ2=makeQuery(id+"F6.imprint","INTERSECT",VERTEX,{"disambiguationData":[OD(0.0)],"derivedFrom":[subQ1,subQ0]});Q36=makeQuery(id+"F6.imprint","IMPRINT",FACE,{"disambiguationData":[TD([[makeQuery(id+"F6.imprint","IMPRINT",EDGE,{"disambiguationData":[TD([[subQ2,-1.0]])],"derivedFrom":subQ1}),1.0]])]});}
            var Q37;
            {var subQ0=sQuery(id+"F6.wireOp",EDGE,"E34");var subQ1=sQuery(id+"F6.wireOp",EDGE,"E24");var subQ2=makeQuery(id+"F6.imprint","INTERSECT",VERTEX,{"disambiguationData":[OD(0.0)],"derivedFrom":[subQ1,subQ0]});Q37=makeQuery(id+"F6.imprint","IMPRINT",FACE,{"disambiguationData":[TD([[makeQuery(id+"F6.imprint","IMPRINT",EDGE,{"disambiguationData":[TD([[subQ2,-1.0]])],"derivedFrom":subQ1}),-1.0]])]});}
            var Q38;
            {var subQ0=sQuery(id+"F6.wireOp",EDGE,"E16");var subQ1=sQuery(id+"F6.wireOp",EDGE,"E15");var subQ2=makeQuery(id+"F6.imprint","INTERSECT",VERTEX,{"derivedFrom":[subQ1,subQ0]});Q38=makeQuery(id+"F6.imprint","IMPRINT",FACE,{"disambiguationData":[TD([[makeQuery(id+"F6.imprint","IMPRINT",EDGE,{"disambiguationData":[TD([[subQ2,1.0]])],"derivedFrom":subQ1}),1.0]])]});}
            var Q39;
            {var subQ0=sQuery(id+"F6.wireOp",EDGE,"E16");var subQ1=sQuery(id+"F6.wireOp",EDGE,"E15");var subQ2=makeQuery(id+"F6.imprint","INTERSECT",VERTEX,{"derivedFrom":[subQ1,subQ0]});Q39=makeQuery(id+"F6.imprint","IMPRINT",FACE,{"disambiguationData":[TD([[makeQuery(id+"F6.imprint","IMPRINT",EDGE,{"disambiguationData":[TD([[subQ2,1.0]])],"derivedFrom":subQ1}),-1.0]])]});}
            var Q40;
            {var subQ0=sQuery(id+"F6.wireOp",EDGE,"E17");var subQ1=sQuery(id+"F6.wireOp",EDGE,"E16");var subQ2=makeQuery(id+"F6.imprint","INTERSECT",VERTEX,{"derivedFrom":[subQ1,subQ0]});Q40=makeQuery(id+"F6.imprint","IMPRINT",FACE,{"disambiguationData":[TD([[makeQuery(id+"F6.imprint","IMPRINT",EDGE,{"disambiguationData":[TD([[subQ2,1.0]])],"derivedFrom":subQ1}),-1.0]])]});}
            var Q41;
            {var subQ0=sQuery(id+"F6.wireOp",EDGE,"E17");var subQ1=sQuery(id+"F6.wireOp",EDGE,"E16");var subQ2=makeQuery(id+"F6.imprint","INTERSECT",VERTEX,{"derivedFrom":[subQ1,subQ0]});Q41=makeQuery(id+"F6.imprint","IMPRINT",FACE,{"disambiguationData":[TD([[makeQuery(id+"F6.imprint","IMPRINT",EDGE,{"disambiguationData":[TD([[subQ2,1.0]])],"derivedFrom":subQ1}),1.0]])]});}
            var Q42;
            {var subQ0=sQuery(id+"F6.wireOp",EDGE,"E35");var subQ1=sQuery(id+"F6.wireOp",EDGE,"E24");var subQ2=makeQuery(id+"F6.imprint","INTERSECT",VERTEX,{"disambiguationData":[OD(0.0)],"derivedFrom":[subQ1,subQ0]});Q42=makeQuery(id+"F6.imprint","IMPRINT",FACE,{"disambiguationData":[TD([[makeQuery(id+"F6.imprint","IMPRINT",EDGE,{"disambiguationData":[TD([[subQ2,-1.0]])],"derivedFrom":subQ1}),-1.0]])]});}
            var Q43;
            {var subQ0=sQuery(id+"F6.wireOp",EDGE,"E35");var subQ1=sQuery(id+"F6.wireOp",EDGE,"E24");var subQ2=makeQuery(id+"F6.imprint","INTERSECT",VERTEX,{"disambiguationData":[OD(0.0)],"derivedFrom":[subQ1,subQ0]});Q43=makeQuery(id+"F6.imprint","IMPRINT",FACE,{"disambiguationData":[TD([[makeQuery(id+"F6.imprint","IMPRINT",EDGE,{"disambiguationData":[TD([[subQ2,-1.0]])],"derivedFrom":subQ1}),1.0]])]});}
            var Q44;
            {var subQ0=sQuery(id+"F6.wireOp",EDGE,"E40.MirrorC");var subQ1=sQuery(id+"F6.wireOp",EDGE,"E25");var subQ2=makeQuery(id+"F6.imprint","INTERSECT",VERTEX,{"disambiguationData":[OD(0.0)],"derivedFrom":[subQ1,subQ0]});Q44=makeQuery(id+"F6.imprint","IMPRINT",FACE,{"disambiguationData":[TD([[makeQuery(id+"F6.imprint","IMPRINT",EDGE,{"disambiguationData":[TD([[subQ2,-1.0]])],"derivedFrom":subQ1}),-1.0]])]});}
            var Q45;
            {var subQ0=sQuery(id+"F6.wireOp",EDGE,"E40.MirrorC");var subQ1=sQuery(id+"F6.wireOp",EDGE,"E25");var subQ2=makeQuery(id+"F6.imprint","INTERSECT",VERTEX,{"disambiguationData":[OD(0.0)],"derivedFrom":[subQ1,subQ0]});Q45=makeQuery(id+"F6.imprint","IMPRINT",FACE,{"disambiguationData":[TD([[makeQuery(id+"F6.imprint","IMPRINT",EDGE,{"disambiguationData":[TD([[subQ2,-1.0]])],"derivedFrom":subQ1}),1.0]])]});}
            var Q46;
            {var subQ0=sQuery(id+"F6.wireOp",EDGE,"E45.MirrorC");var subQ1=sQuery(id+"F6.wireOp",EDGE,"E26");var subQ2=makeQuery(id+"F6.imprint","INTERSECT",VERTEX,{"disambiguationData":[OD(0.0)],"derivedFrom":[subQ1,subQ0]});Q46=makeQuery(id+"F6.imprint","IMPRINT",FACE,{"disambiguationData":[TD([[makeQuery(id+"F6.imprint","IMPRINT",EDGE,{"disambiguationData":[TD([[subQ2,-1.0]])],"derivedFrom":subQ1}),-1.0]])]});}
            var Q47;
            {var subQ0=sQuery(id+"F6.wireOp",EDGE,"E45.MirrorC");var subQ1=sQuery(id+"F6.wireOp",EDGE,"E26");var subQ2=makeQuery(id+"F6.imprint","INTERSECT",VERTEX,{"disambiguationData":[OD(0.0)],"derivedFrom":[subQ1,subQ0]});Q47=makeQuery(id+"F6.imprint","IMPRINT",FACE,{"disambiguationData":[TD([[makeQuery(id+"F6.imprint","IMPRINT",EDGE,{"disambiguationData":[TD([[subQ2,-1.0]])],"derivedFrom":subQ1}),1.0]])]});}
            var Q48;
            {var subQ0=sQuery(id+"F6.wireOp",EDGE,"E50.MirrorC");var subQ1=sQuery(id+"F6.wireOp",EDGE,"E27");var subQ2=makeQuery(id+"F6.imprint","INTERSECT",VERTEX,{"disambiguationData":[OD(0.0)],"derivedFrom":[subQ1,subQ0]});Q48=makeQuery(id+"F6.imprint","IMPRINT",FACE,{"disambiguationData":[TD([[makeQuery(id+"F6.imprint","IMPRINT",EDGE,{"disambiguationData":[TD([[subQ2,-1.0]])],"derivedFrom":subQ1}),1.0]])]});}
            var Q49;
            {var subQ0=sQuery(id+"F6.wireOp",EDGE,"E50.MirrorC");var subQ1=sQuery(id+"F6.wireOp",EDGE,"E27");var subQ2=makeQuery(id+"F6.imprint","INTERSECT",VERTEX,{"disambiguationData":[OD(0.0)],"derivedFrom":[subQ1,subQ0]});Q49=makeQuery(id+"F6.imprint","IMPRINT",FACE,{"disambiguationData":[TD([[makeQuery(id+"F6.imprint","IMPRINT",EDGE,{"disambiguationData":[TD([[subQ2,-1.0]])],"derivedFrom":subQ1}),-1.0]])]});}
            var Q50;
            {var subQ0=sQuery(id+"F6.wireOp",EDGE,"E59.MirrorC");var subQ1=sQuery(id+"F6.wireOp",EDGE,"E28");var subQ2=makeQuery(id+"F6.imprint","INTERSECT",VERTEX,{"disambiguationData":[OD(0.0)],"derivedFrom":[subQ1,subQ0]});Q50=makeQuery(id+"F6.imprint","IMPRINT",FACE,{"disambiguationData":[TD([[makeQuery(id+"F6.imprint","IMPRINT",EDGE,{"disambiguationData":[TD([[subQ2,-1.0]])],"derivedFrom":subQ1}),-1.0]])]});}
            var Q51;
            {var subQ0=sQuery(id+"F6.wireOp",EDGE,"E59.MirrorC");var subQ1=sQuery(id+"F6.wireOp",EDGE,"E28");var subQ2=makeQuery(id+"F6.imprint","INTERSECT",VERTEX,{"disambiguationData":[OD(0.0)],"derivedFrom":[subQ1,subQ0]});Q51=makeQuery(id+"F6.imprint","IMPRINT",FACE,{"disambiguationData":[TD([[makeQuery(id+"F6.imprint","IMPRINT",EDGE,{"disambiguationData":[TD([[subQ2,-1.0]])],"derivedFrom":subQ1}),1.0]])]});}
            var Q52;
            {var subQ0=sQuery(id+"F6.wireOp",EDGE,"E55.MirrorC");var subQ1=sQuery(id+"F6.wireOp",EDGE,"E29");var subQ2=makeQuery(id+"F6.imprint","INTERSECT",VERTEX,{"disambiguationData":[OD(0.0)],"derivedFrom":[subQ1,subQ0]});Q52=makeQuery(id+"F6.imprint","IMPRINT",FACE,{"disambiguationData":[TD([[makeQuery(id+"F6.imprint","IMPRINT",EDGE,{"disambiguationData":[TD([[subQ2,-1.0]])],"derivedFrom":subQ1}),1.0]])]});}
            var Q53;
            {var subQ0=sQuery(id+"F6.wireOp",EDGE,"E55.MirrorC");var subQ1=sQuery(id+"F6.wireOp",EDGE,"E29");var subQ2=makeQuery(id+"F6.imprint","INTERSECT",VERTEX,{"disambiguationData":[OD(0.0)],"derivedFrom":[subQ1,subQ0]});Q53=makeQuery(id+"F6.imprint","IMPRINT",FACE,{"disambiguationData":[TD([[makeQuery(id+"F6.imprint","IMPRINT",EDGE,{"disambiguationData":[TD([[subQ2,-1.0]])],"derivedFrom":subQ1}),-1.0]])]});}
            var Q54;
            {var subQ0=sQuery(id+"F6.wireOp",EDGE,"E65.MirrorC");var subQ1=sQuery(id+"F6.wireOp",EDGE,"E31");var subQ2=makeQuery(id+"F6.imprint","INTERSECT",VERTEX,{"disambiguationData":[OD(0.0)],"derivedFrom":[subQ1,subQ0]});Q54=makeQuery(id+"F6.imprint","IMPRINT",FACE,{"disambiguationData":[TD([[makeQuery(id+"F6.imprint","IMPRINT",EDGE,{"disambiguationData":[TD([[subQ2,-1.0]])],"derivedFrom":subQ1}),-1.0]])]});}
            var Q55;
            {var subQ0=sQuery(id+"F6.wireOp",EDGE,"E65.MirrorC");var subQ1=sQuery(id+"F6.wireOp",EDGE,"E31");var subQ2=makeQuery(id+"F6.imprint","INTERSECT",VERTEX,{"disambiguationData":[OD(0.0)],"derivedFrom":[subQ1,subQ0]});Q55=makeQuery(id+"F6.imprint","IMPRINT",FACE,{"disambiguationData":[TD([[makeQuery(id+"F6.imprint","IMPRINT",EDGE,{"disambiguationData":[TD([[subQ2,-1.0]])],"derivedFrom":subQ1}),1.0]])]});}
            var Q56;
            {var subQ0=sQuery(id+"F6.wireOp",EDGE,"E70.MirrorC");var subQ1=sQuery(id+"F6.wireOp",EDGE,"E30");var subQ2=makeQuery(id+"F6.imprint","INTERSECT",VERTEX,{"disambiguationData":[OD(0.0)],"derivedFrom":[subQ1,subQ0]});Q56=makeQuery(id+"F6.imprint","IMPRINT",FACE,{"disambiguationData":[TD([[makeQuery(id+"F6.imprint","IMPRINT",EDGE,{"disambiguationData":[TD([[subQ2,-1.0]])],"derivedFrom":subQ1}),-1.0]])]});}
            var Q57;
            {var subQ0=sQuery(id+"F6.wireOp",EDGE,"E70.MirrorC");var subQ1=sQuery(id+"F6.wireOp",EDGE,"E30");var subQ2=makeQuery(id+"F6.imprint","INTERSECT",VERTEX,{"disambiguationData":[OD(0.0)],"derivedFrom":[subQ1,subQ0]});Q57=makeQuery(id+"F6.imprint","IMPRINT",FACE,{"disambiguationData":[TD([[makeQuery(id+"F6.imprint","IMPRINT",EDGE,{"disambiguationData":[TD([[subQ2,-1.0]])],"derivedFrom":subQ1}),1.0]])]});}
            var Q58;
            {var subQ0=sQuery(id+"F6.wireOp",EDGE,"E75.MirrorC");var subQ1=sQuery(id+"F6.wireOp",EDGE,"E32");var subQ2=makeQuery(id+"F6.imprint","INTERSECT",VERTEX,{"disambiguationData":[OD(0.0)],"derivedFrom":[subQ1,subQ0]});Q58=makeQuery(id+"F6.imprint","IMPRINT",FACE,{"disambiguationData":[TD([[makeQuery(id+"F6.imprint","IMPRINT",EDGE,{"disambiguationData":[TD([[subQ2,-1.0]])],"derivedFrom":subQ1}),-1.0]])]});}
            var Q59;
            {var subQ0=sQuery(id+"F6.wireOp",EDGE,"E75.MirrorC");var subQ1=sQuery(id+"F6.wireOp",EDGE,"E32");var subQ2=makeQuery(id+"F6.imprint","INTERSECT",VERTEX,{"disambiguationData":[OD(0.0)],"derivedFrom":[subQ1,subQ0]});Q59=makeQuery(id+"F6.imprint","IMPRINT",FACE,{"disambiguationData":[TD([[makeQuery(id+"F6.imprint","IMPRINT",EDGE,{"disambiguationData":[TD([[subQ2,-1.0]])],"derivedFrom":subQ1}),1.0]])]});}
            var Q60;
            {var subQ0=sQuery(id+"F6.wireOp",EDGE,"E76.MirrorC");var subQ1=sQuery(id+"F6.wireOp",EDGE,"E32");var subQ2=makeQuery(id+"F6.imprint","INTERSECT",VERTEX,{"disambiguationData":[OD(0.0)],"derivedFrom":[subQ1,subQ0]});Q60=makeQuery(id+"F6.imprint","IMPRINT",FACE,{"disambiguationData":[TD([[makeQuery(id+"F6.imprint","IMPRINT",EDGE,{"disambiguationData":[TD([[subQ2,-1.0]])],"derivedFrom":subQ1}),1.0]])]});}
            var Q61;
            {var subQ0=sQuery(id+"F6.wireOp",EDGE,"E76.MirrorC");var subQ1=sQuery(id+"F6.wireOp",EDGE,"E32");var subQ2=makeQuery(id+"F6.imprint","INTERSECT",VERTEX,{"disambiguationData":[OD(0.0)],"derivedFrom":[subQ1,subQ0]});Q61=makeQuery(id+"F6.imprint","IMPRINT",FACE,{"disambiguationData":[TD([[makeQuery(id+"F6.imprint","IMPRINT",EDGE,{"disambiguationData":[TD([[subQ2,-1.0]])],"derivedFrom":subQ1}),-1.0]])]});}
            var Q62;
            {var subQ0=sQuery(id+"F6.wireOp",EDGE,"E71.MirrorC");var subQ1=sQuery(id+"F6.wireOp",EDGE,"E30");var subQ2=makeQuery(id+"F6.imprint","INTERSECT",VERTEX,{"disambiguationData":[OD(0.0)],"derivedFrom":[subQ1,subQ0]});Q62=makeQuery(id+"F6.imprint","IMPRINT",FACE,{"disambiguationData":[TD([[makeQuery(id+"F6.imprint","IMPRINT",EDGE,{"disambiguationData":[TD([[subQ2,-1.0]])],"derivedFrom":subQ1}),1.0]])]});}
            var Q63;
            {var subQ0=sQuery(id+"F6.wireOp",EDGE,"E71.MirrorC");var subQ1=sQuery(id+"F6.wireOp",EDGE,"E30");var subQ2=makeQuery(id+"F6.imprint","INTERSECT",VERTEX,{"disambiguationData":[OD(0.0)],"derivedFrom":[subQ1,subQ0]});Q63=makeQuery(id+"F6.imprint","IMPRINT",FACE,{"disambiguationData":[TD([[makeQuery(id+"F6.imprint","IMPRINT",EDGE,{"disambiguationData":[TD([[subQ2,-1.0]])],"derivedFrom":subQ1}),-1.0]])]});}
            var Q64;
            {var subQ0=sQuery(id+"F6.wireOp",EDGE,"E66.MirrorC");var subQ1=sQuery(id+"F6.wireOp",EDGE,"E31");var subQ2=makeQuery(id+"F6.imprint","INTERSECT",VERTEX,{"disambiguationData":[OD(0.0)],"derivedFrom":[subQ1,subQ0]});Q64=makeQuery(id+"F6.imprint","IMPRINT",FACE,{"disambiguationData":[TD([[makeQuery(id+"F6.imprint","IMPRINT",EDGE,{"disambiguationData":[TD([[subQ2,-1.0]])],"derivedFrom":subQ1}),1.0]])]});}
            var Q65;
            {var subQ0=sQuery(id+"F6.wireOp",EDGE,"E66.MirrorC");var subQ1=sQuery(id+"F6.wireOp",EDGE,"E31");var subQ2=makeQuery(id+"F6.imprint","INTERSECT",VERTEX,{"disambiguationData":[OD(0.0)],"derivedFrom":[subQ1,subQ0]});Q65=makeQuery(id+"F6.imprint","IMPRINT",FACE,{"disambiguationData":[TD([[makeQuery(id+"F6.imprint","IMPRINT",EDGE,{"disambiguationData":[TD([[subQ2,-1.0]])],"derivedFrom":subQ1}),-1.0]])]});}
            var Q66;
            {var subQ0=sQuery(id+"F6.wireOp",EDGE,"E56.MirrorC");var subQ1=sQuery(id+"F6.wireOp",EDGE,"E29");var subQ2=makeQuery(id+"F6.imprint","INTERSECT",VERTEX,{"disambiguationData":[OD(0.0)],"derivedFrom":[subQ1,subQ0]});Q66=makeQuery(id+"F6.imprint","IMPRINT",FACE,{"disambiguationData":[TD([[makeQuery(id+"F6.imprint","IMPRINT",EDGE,{"disambiguationData":[TD([[subQ2,-1.0]])],"derivedFrom":subQ1}),-1.0]])]});}
            var Q67;
            {var subQ0=sQuery(id+"F6.wireOp",EDGE,"E56.MirrorC");var subQ1=sQuery(id+"F6.wireOp",EDGE,"E29");var subQ2=makeQuery(id+"F6.imprint","INTERSECT",VERTEX,{"disambiguationData":[OD(0.0)],"derivedFrom":[subQ1,subQ0]});Q67=makeQuery(id+"F6.imprint","IMPRINT",FACE,{"disambiguationData":[TD([[makeQuery(id+"F6.imprint","IMPRINT",EDGE,{"disambiguationData":[TD([[subQ2,-1.0]])],"derivedFrom":subQ1}),1.0]])]});}
            var Q68;
            {var subQ0=sQuery(id+"F6.wireOp",EDGE,"E61.MirrorC");var subQ1=sQuery(id+"F6.wireOp",EDGE,"E28");var subQ2=makeQuery(id+"F6.imprint","INTERSECT",VERTEX,{"disambiguationData":[OD(0.0)],"derivedFrom":[subQ1,subQ0]});Q68=makeQuery(id+"F6.imprint","IMPRINT",FACE,{"disambiguationData":[TD([[makeQuery(id+"F6.imprint","IMPRINT",EDGE,{"disambiguationData":[TD([[subQ2,-1.0]])],"derivedFrom":subQ1}),1.0]])]});}
            var Q69;
            {var subQ0=sQuery(id+"F6.wireOp",EDGE,"E61.MirrorC");var subQ1=sQuery(id+"F6.wireOp",EDGE,"E28");var subQ2=makeQuery(id+"F6.imprint","INTERSECT",VERTEX,{"disambiguationData":[OD(0.0)],"derivedFrom":[subQ1,subQ0]});Q69=makeQuery(id+"F6.imprint","IMPRINT",FACE,{"disambiguationData":[TD([[makeQuery(id+"F6.imprint","IMPRINT",EDGE,{"disambiguationData":[TD([[subQ2,-1.0]])],"derivedFrom":subQ1}),-1.0]])]});}
            var Q70;
            {var subQ0=sQuery(id+"F6.wireOp",EDGE,"E52.MirrorC");var subQ1=sQuery(id+"F6.wireOp",EDGE,"E27");var subQ2=makeQuery(id+"F6.imprint","INTERSECT",VERTEX,{"disambiguationData":[OD(0.0)],"derivedFrom":[subQ1,subQ0]});Q70=makeQuery(id+"F6.imprint","IMPRINT",FACE,{"disambiguationData":[TD([[makeQuery(id+"F6.imprint","IMPRINT",EDGE,{"disambiguationData":[TD([[subQ2,-1.0]])],"derivedFrom":subQ1}),-1.0]])]});}
            var Q71;
            {var subQ0=sQuery(id+"F6.wireOp",EDGE,"E52.MirrorC");var subQ1=sQuery(id+"F6.wireOp",EDGE,"E27");var subQ2=makeQuery(id+"F6.imprint","INTERSECT",VERTEX,{"disambiguationData":[OD(0.0)],"derivedFrom":[subQ1,subQ0]});Q71=makeQuery(id+"F6.imprint","IMPRINT",FACE,{"disambiguationData":[TD([[makeQuery(id+"F6.imprint","IMPRINT",EDGE,{"disambiguationData":[TD([[subQ2,-1.0]])],"derivedFrom":subQ1}),1.0]])]});}
            var Q72;
            {var subQ0=sQuery(id+"F6.wireOp",EDGE,"E46.MirrorC");var subQ1=sQuery(id+"F6.wireOp",EDGE,"E26");var subQ2=makeQuery(id+"F6.imprint","INTERSECT",VERTEX,{"disambiguationData":[OD(0.0)],"derivedFrom":[subQ1,subQ0]});Q72=makeQuery(id+"F6.imprint","IMPRINT",FACE,{"disambiguationData":[TD([[makeQuery(id+"F6.imprint","IMPRINT",EDGE,{"disambiguationData":[TD([[subQ2,-1.0]])],"derivedFrom":subQ1}),1.0]])]});}
            var Q73;
            {var subQ0=sQuery(id+"F6.wireOp",EDGE,"E46.MirrorC");var subQ1=sQuery(id+"F6.wireOp",EDGE,"E26");var subQ2=makeQuery(id+"F6.imprint","INTERSECT",VERTEX,{"disambiguationData":[OD(0.0)],"derivedFrom":[subQ1,subQ0]});Q73=makeQuery(id+"F6.imprint","IMPRINT",FACE,{"disambiguationData":[TD([[makeQuery(id+"F6.imprint","IMPRINT",EDGE,{"disambiguationData":[TD([[subQ2,-1.0]])],"derivedFrom":subQ1}),-1.0]])]});}
            var Q74;
            {var subQ0=sQuery(id+"F6.wireOp",EDGE,"E41.MirrorC");var subQ1=sQuery(id+"F6.wireOp",EDGE,"E25");var subQ2=makeQuery(id+"F6.imprint","INTERSECT",VERTEX,{"disambiguationData":[OD(0.0)],"derivedFrom":[subQ1,subQ0]});Q74=makeQuery(id+"F6.imprint","IMPRINT",FACE,{"disambiguationData":[TD([[makeQuery(id+"F6.imprint","IMPRINT",EDGE,{"disambiguationData":[TD([[subQ2,-1.0]])],"derivedFrom":subQ1}),1.0]])]});}
            var Q75;
            {var subQ0=sQuery(id+"F6.wireOp",EDGE,"E41.MirrorC");var subQ1=sQuery(id+"F6.wireOp",EDGE,"E25");var subQ2=makeQuery(id+"F6.imprint","INTERSECT",VERTEX,{"disambiguationData":[OD(0.0)],"derivedFrom":[subQ1,subQ0]});Q75=makeQuery(id+"F6.imprint","IMPRINT",FACE,{"disambiguationData":[TD([[makeQuery(id+"F6.imprint","IMPRINT",EDGE,{"disambiguationData":[TD([[subQ2,-1.0]])],"derivedFrom":subQ1}),-1.0]])]});}
            var Q76;
            {var subQ0=sQuery(id+"F6.wireOp",EDGE,"E36");var subQ1=sQuery(id+"F6.wireOp",EDGE,"E24");var subQ2=makeQuery(id+"F6.imprint","INTERSECT",VERTEX,{"disambiguationData":[OD(0.0)],"derivedFrom":[subQ1,subQ0]});Q76=makeQuery(id+"F6.imprint","IMPRINT",FACE,{"disambiguationData":[TD([[makeQuery(id+"F6.imprint","IMPRINT",EDGE,{"disambiguationData":[TD([[subQ2,-1.0]])],"derivedFrom":subQ1}),1.0]])]});}
            var Q77;
            {var subQ0=sQuery(id+"F6.wireOp",EDGE,"E36");var subQ1=sQuery(id+"F6.wireOp",EDGE,"E24");var subQ2=makeQuery(id+"F6.imprint","INTERSECT",VERTEX,{"disambiguationData":[OD(0.0)],"derivedFrom":[subQ1,subQ0]});Q77=makeQuery(id+"F6.imprint","IMPRINT",FACE,{"disambiguationData":[TD([[makeQuery(id+"F6.imprint","IMPRINT",EDGE,{"disambiguationData":[TD([[subQ2,-1.0]])],"derivedFrom":subQ1}),-1.0]])]});}
            var Q78;
            {var subQ0=sQuery(id+"F6.wireOp",EDGE,"E18");var subQ1=sQuery(id+"F6.wireOp",EDGE,"E17");var subQ2=makeQuery(id+"F6.imprint","INTERSECT",VERTEX,{"derivedFrom":[subQ1,subQ0]});Q78=makeQuery(id+"F6.imprint","IMPRINT",FACE,{"disambiguationData":[TD([[makeQuery(id+"F6.imprint","IMPRINT",EDGE,{"disambiguationData":[TD([[subQ2,1.0]])],"derivedFrom":subQ1}),1.0]])]});}
            var Q79;
            {var subQ0=sQuery(id+"F6.wireOp",EDGE,"E18");var subQ1=sQuery(id+"F6.wireOp",EDGE,"E17");var subQ2=makeQuery(id+"F6.imprint","INTERSECT",VERTEX,{"derivedFrom":[subQ1,subQ0]});Q79=makeQuery(id+"F6.imprint","IMPRINT",FACE,{"disambiguationData":[TD([[makeQuery(id+"F6.imprint","IMPRINT",EDGE,{"disambiguationData":[TD([[subQ2,1.0]])],"derivedFrom":subQ1}),-1.0]])]});}
            var Q80;
            Q80=makeQuery(id+"F6.imprint","IMPRINT",FACE,{"disambiguationData":[TD([[makeQuery(id+"F6.imprint","IMPRINT",EDGE,{"derivedFrom":sQuery(id+"F6.wireOp",EDGE,"E23")}),1.0]])]});
            var Q81;
            {var subQ0=sQuery(id+"F6.wireOp",EDGE,"E37");var subQ1=sQuery(id+"F6.wireOp",EDGE,"E24");var subQ2=makeQuery(id+"F6.imprint","INTERSECT",VERTEX,{"disambiguationData":[OD(0.0)],"derivedFrom":[subQ1,subQ0]});Q81=makeQuery(id+"F6.imprint","IMPRINT",FACE,{"disambiguationData":[TD([[makeQuery(id+"F6.imprint","IMPRINT",EDGE,{"disambiguationData":[TD([[subQ2,-1.0]])],"derivedFrom":subQ1}),-1.0]])]});}
            var Q82;
            {var subQ0=sQuery(id+"F6.wireOp",EDGE,"E37");var subQ1=sQuery(id+"F6.wireOp",EDGE,"E24");var subQ2=makeQuery(id+"F6.imprint","INTERSECT",VERTEX,{"disambiguationData":[OD(0.0)],"derivedFrom":[subQ1,subQ0]});Q82=makeQuery(id+"F6.imprint","IMPRINT",FACE,{"disambiguationData":[TD([[makeQuery(id+"F6.imprint","IMPRINT",EDGE,{"disambiguationData":[TD([[subQ2,-1.0]])],"derivedFrom":subQ1}),1.0]])]});}
            var Q83;
            {var subQ0=sQuery(id+"F6.wireOp",EDGE,"E42.MirrorC");var subQ1=sQuery(id+"F6.wireOp",EDGE,"E25");var subQ2=makeQuery(id+"F6.imprint","INTERSECT",VERTEX,{"disambiguationData":[OD(0.0)],"derivedFrom":[subQ1,subQ0]});Q83=makeQuery(id+"F6.imprint","IMPRINT",FACE,{"disambiguationData":[TD([[makeQuery(id+"F6.imprint","IMPRINT",EDGE,{"disambiguationData":[TD([[subQ2,-1.0]])],"derivedFrom":subQ1}),-1.0]])]});}
            var Q84;
            {var subQ0=sQuery(id+"F6.wireOp",EDGE,"E42.MirrorC");var subQ1=sQuery(id+"F6.wireOp",EDGE,"E25");var subQ2=makeQuery(id+"F6.imprint","INTERSECT",VERTEX,{"disambiguationData":[OD(0.0)],"derivedFrom":[subQ1,subQ0]});Q84=makeQuery(id+"F6.imprint","IMPRINT",FACE,{"disambiguationData":[TD([[makeQuery(id+"F6.imprint","IMPRINT",EDGE,{"disambiguationData":[TD([[subQ2,-1.0]])],"derivedFrom":subQ1}),1.0]])]});}
            var Q85;
            {var subQ0=sQuery(id+"F6.wireOp",EDGE,"E47.MirrorC");var subQ1=sQuery(id+"F6.wireOp",EDGE,"E26");var subQ2=makeQuery(id+"F6.imprint","INTERSECT",VERTEX,{"disambiguationData":[OD(0.0)],"derivedFrom":[subQ1,subQ0]});Q85=makeQuery(id+"F6.imprint","IMPRINT",FACE,{"disambiguationData":[TD([[makeQuery(id+"F6.imprint","IMPRINT",EDGE,{"disambiguationData":[TD([[subQ2,-1.0]])],"derivedFrom":subQ1}),-1.0]])]});}
            var Q86;
            {var subQ0=sQuery(id+"F6.wireOp",EDGE,"E47.MirrorC");var subQ1=sQuery(id+"F6.wireOp",EDGE,"E26");var subQ2=makeQuery(id+"F6.imprint","INTERSECT",VERTEX,{"disambiguationData":[OD(0.0)],"derivedFrom":[subQ1,subQ0]});Q86=makeQuery(id+"F6.imprint","IMPRINT",FACE,{"disambiguationData":[TD([[makeQuery(id+"F6.imprint","IMPRINT",EDGE,{"disambiguationData":[TD([[subQ2,-1.0]])],"derivedFrom":subQ1}),1.0]])]});}
            var Q87;
            {var subQ0=sQuery(id+"F6.wireOp",EDGE,"E51.MirrorC");var subQ1=sQuery(id+"F6.wireOp",EDGE,"E27");var subQ2=makeQuery(id+"F6.imprint","INTERSECT",VERTEX,{"disambiguationData":[OD(0.0)],"derivedFrom":[subQ1,subQ0]});Q87=makeQuery(id+"F6.imprint","IMPRINT",FACE,{"disambiguationData":[TD([[makeQuery(id+"F6.imprint","IMPRINT",EDGE,{"disambiguationData":[TD([[subQ2,-1.0]])],"derivedFrom":subQ1}),1.0]])]});}
            var Q88;
            {var subQ0=sQuery(id+"F6.wireOp",EDGE,"E51.MirrorC");var subQ1=sQuery(id+"F6.wireOp",EDGE,"E27");var subQ2=makeQuery(id+"F6.imprint","INTERSECT",VERTEX,{"disambiguationData":[OD(0.0)],"derivedFrom":[subQ1,subQ0]});Q88=makeQuery(id+"F6.imprint","IMPRINT",FACE,{"disambiguationData":[TD([[makeQuery(id+"F6.imprint","IMPRINT",EDGE,{"disambiguationData":[TD([[subQ2,-1.0]])],"derivedFrom":subQ1}),-1.0]])]});}
            var Q89;
            {var subQ0=sQuery(id+"F6.wireOp",EDGE,"E62.MirrorC");var subQ1=sQuery(id+"F6.wireOp",EDGE,"E28");var subQ2=makeQuery(id+"F6.imprint","INTERSECT",VERTEX,{"disambiguationData":[OD(0.0)],"derivedFrom":[subQ1,subQ0]});Q89=makeQuery(id+"F6.imprint","IMPRINT",FACE,{"disambiguationData":[TD([[makeQuery(id+"F6.imprint","IMPRINT",EDGE,{"disambiguationData":[TD([[subQ2,-1.0]])],"derivedFrom":subQ1}),-1.0]])]});}
            var Q90;
            {var subQ0=sQuery(id+"F6.wireOp",EDGE,"E62.MirrorC");var subQ1=sQuery(id+"F6.wireOp",EDGE,"E28");var subQ2=makeQuery(id+"F6.imprint","INTERSECT",VERTEX,{"disambiguationData":[OD(0.0)],"derivedFrom":[subQ1,subQ0]});Q90=makeQuery(id+"F6.imprint","IMPRINT",FACE,{"disambiguationData":[TD([[makeQuery(id+"F6.imprint","IMPRINT",EDGE,{"disambiguationData":[TD([[subQ2,-1.0]])],"derivedFrom":subQ1}),1.0]])]});}
            var Q91;
            {var subQ0=sQuery(id+"F6.wireOp",EDGE,"E57.MirrorC");var subQ1=sQuery(id+"F6.wireOp",EDGE,"E29");var subQ2=makeQuery(id+"F6.imprint","INTERSECT",VERTEX,{"disambiguationData":[OD(0.0)],"derivedFrom":[subQ1,subQ0]});Q91=makeQuery(id+"F6.imprint","IMPRINT",FACE,{"disambiguationData":[TD([[makeQuery(id+"F6.imprint","IMPRINT",EDGE,{"disambiguationData":[TD([[subQ2,-1.0]])],"derivedFrom":subQ1}),1.0]])]});}
            var Q92;
            {var subQ0=sQuery(id+"F6.wireOp",EDGE,"E57.MirrorC");var subQ1=sQuery(id+"F6.wireOp",EDGE,"E29");var subQ2=makeQuery(id+"F6.imprint","INTERSECT",VERTEX,{"disambiguationData":[OD(0.0)],"derivedFrom":[subQ1,subQ0]});Q92=makeQuery(id+"F6.imprint","IMPRINT",FACE,{"disambiguationData":[TD([[makeQuery(id+"F6.imprint","IMPRINT",EDGE,{"disambiguationData":[TD([[subQ2,-1.0]])],"derivedFrom":subQ1}),-1.0]])]});}
            var Q93;
            {var subQ0=sQuery(id+"F6.wireOp",EDGE,"E67.MirrorC");var subQ1=sQuery(id+"F6.wireOp",EDGE,"E31");var subQ2=makeQuery(id+"F6.imprint","INTERSECT",VERTEX,{"disambiguationData":[OD(0.0)],"derivedFrom":[subQ1,subQ0]});Q93=makeQuery(id+"F6.imprint","IMPRINT",FACE,{"disambiguationData":[TD([[makeQuery(id+"F6.imprint","IMPRINT",EDGE,{"disambiguationData":[TD([[subQ2,-1.0]])],"derivedFrom":subQ1}),-1.0]])]});}
            var Q94;
            {var subQ0=sQuery(id+"F6.wireOp",EDGE,"E67.MirrorC");var subQ1=sQuery(id+"F6.wireOp",EDGE,"E31");var subQ2=makeQuery(id+"F6.imprint","INTERSECT",VERTEX,{"disambiguationData":[OD(0.0)],"derivedFrom":[subQ1,subQ0]});Q94=makeQuery(id+"F6.imprint","IMPRINT",FACE,{"disambiguationData":[TD([[makeQuery(id+"F6.imprint","IMPRINT",EDGE,{"disambiguationData":[TD([[subQ2,-1.0]])],"derivedFrom":subQ1}),1.0]])]});}
            var Q95;
            {var subQ0=sQuery(id+"F6.wireOp",EDGE,"E72.MirrorC");var subQ1=sQuery(id+"F6.wireOp",EDGE,"E30");var subQ2=makeQuery(id+"F6.imprint","INTERSECT",VERTEX,{"disambiguationData":[OD(0.0)],"derivedFrom":[subQ1,subQ0]});Q95=makeQuery(id+"F6.imprint","IMPRINT",FACE,{"disambiguationData":[TD([[makeQuery(id+"F6.imprint","IMPRINT",EDGE,{"disambiguationData":[TD([[subQ2,-1.0]])],"derivedFrom":subQ1}),-1.0]])]});}
            var Q96;
            {var subQ0=sQuery(id+"F6.wireOp",EDGE,"E72.MirrorC");var subQ1=sQuery(id+"F6.wireOp",EDGE,"E30");var subQ2=makeQuery(id+"F6.imprint","INTERSECT",VERTEX,{"disambiguationData":[OD(0.0)],"derivedFrom":[subQ1,subQ0]});Q96=makeQuery(id+"F6.imprint","IMPRINT",FACE,{"disambiguationData":[TD([[makeQuery(id+"F6.imprint","IMPRINT",EDGE,{"disambiguationData":[TD([[subQ2,-1.0]])],"derivedFrom":subQ1}),1.0]])]});}
            var Q97;
            {var subQ0=sQuery(id+"F6.wireOp",EDGE,"E77.MirrorC");var subQ1=sQuery(id+"F6.wireOp",EDGE,"E32");var subQ2=makeQuery(id+"F6.imprint","INTERSECT",VERTEX,{"disambiguationData":[OD(0.0)],"derivedFrom":[subQ1,subQ0]});Q97=makeQuery(id+"F6.imprint","IMPRINT",FACE,{"disambiguationData":[TD([[makeQuery(id+"F6.imprint","IMPRINT",EDGE,{"disambiguationData":[TD([[subQ2,-1.0]])],"derivedFrom":subQ1}),-1.0]])]});}
            var Q98;
            {var subQ0=sQuery(id+"F6.wireOp",EDGE,"E77.MirrorC");var subQ1=sQuery(id+"F6.wireOp",EDGE,"E32");var subQ2=makeQuery(id+"F6.imprint","INTERSECT",VERTEX,{"disambiguationData":[OD(0.0)],"derivedFrom":[subQ1,subQ0]});Q98=makeQuery(id+"F6.imprint","IMPRINT",FACE,{"disambiguationData":[TD([[makeQuery(id+"F6.imprint","IMPRINT",EDGE,{"disambiguationData":[TD([[subQ2,-1.0]])],"derivedFrom":subQ1}),1.0]])]});}
            extrude(context, id + "F7", {"entities" : qUnion([Q0, Q1, Q2, Q3, Q4, Q5, Q6, Q7, Q8, Q9, Q10, Q11, Q12, Q13, Q14, Q15, Q16, Q17, Q18, Q19, Q20, Q21, Q22, Q23, Q24, Q25, Q26, Q27, Q28, Q29, Q30, Q31, Q32, Q33, Q34, Q35, Q36, Q37, Q38, Q39, Q40, Q41, Q42, Q43, Q44, Q45, Q46, Q47, Q48, Q49, Q50, Q51, Q52, Q53, Q54, Q55, Q56, Q57, Q58, Q59, Q60, Q61, Q62, Q63, Q64, Q65, Q66, Q67, Q68, Q69, Q70, Q71, Q72, Q73, Q74, Q75, Q76, Q77, Q78, Q79, Q80, Q81, Q82, Q83, Q84, Q85, Q86, Q87, Q88, Q89, Q90, Q91, Q92, Q93, Q94, Q95, Q96, Q97, Q98]), "operationType" : NewBodyOperationType.REMOVE, "oppositeDirection" : true, "depth" : 25 * mm, "offsetDistance" : 25 * mm});
        }
    });
